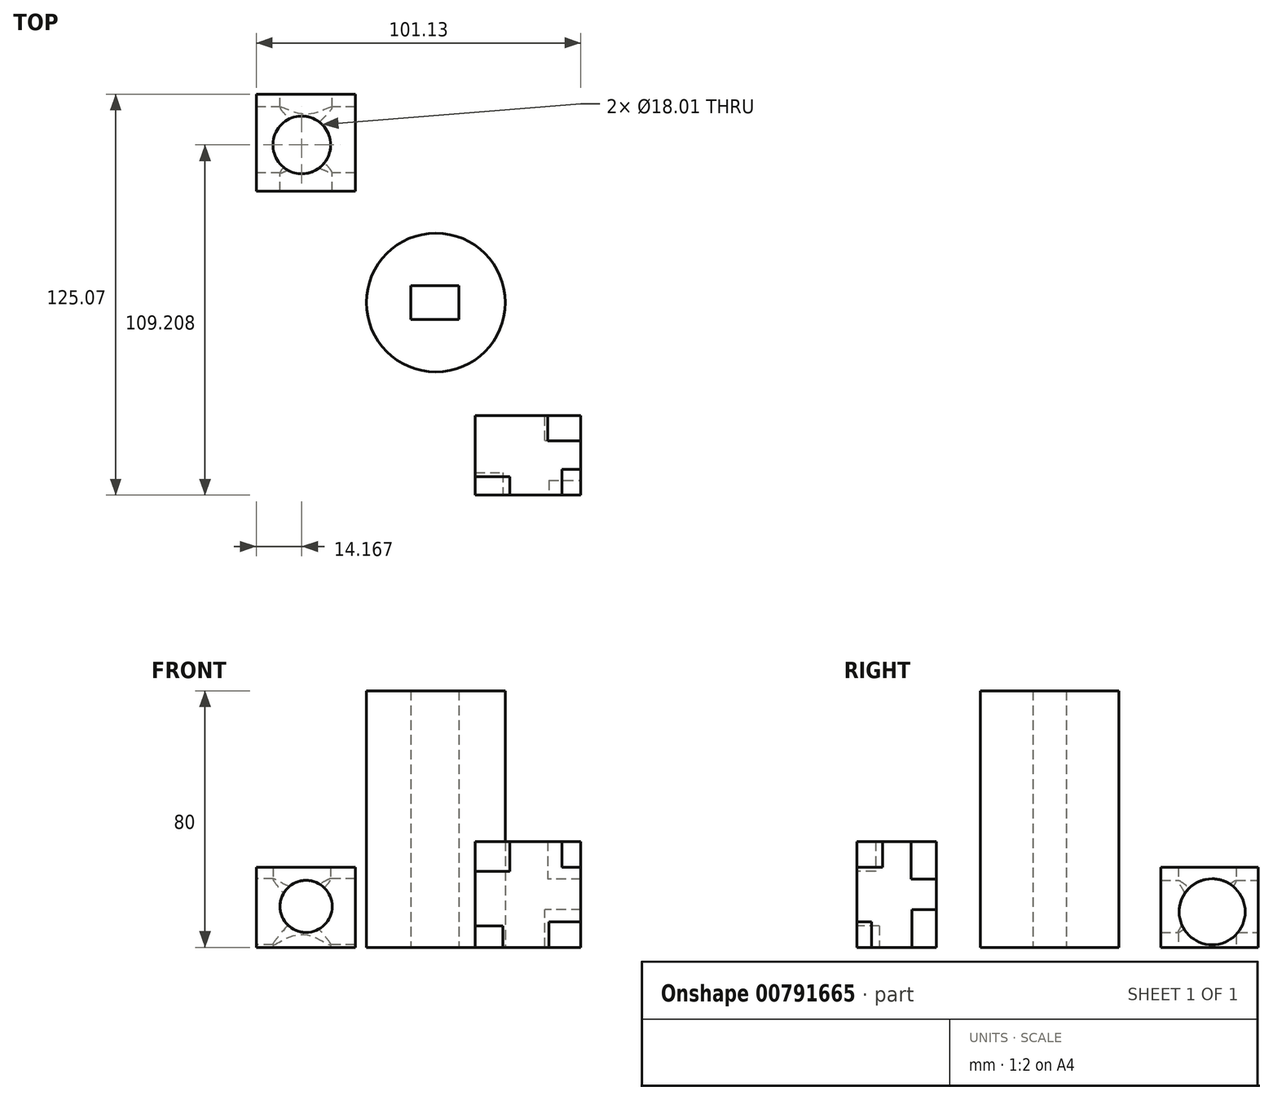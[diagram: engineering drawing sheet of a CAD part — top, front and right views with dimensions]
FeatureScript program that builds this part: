
annotation { "Feature Type Name" : "Feature", "Feature Type Description" : "" }
export const myFeature = defineFeature(function(context is Context, id is Id, definition is map)
    precondition{}
    {
        {
            var Q0;
            Q0=qCreatedBy(makeId("Top.planeOp"),FACE);
            var sketch = newSketch(context, id + "F0", { "sketchPlane" : qUnion([Q0])});
            skCircle(sketch, "E0", {"center": v(0, 0) * mm, "radius": 21.63 * mm});
            skLineSegment(sketch, "E1.bottom", {"start": v(-7.8, 5.24) * mm, "end": v(7.22, 5.24) * mm});
            skLineSegment(sketch, "E1.top", {"start": v(-7.8, -5.24) * mm, "end": v(7.22, -5.24) * mm});
            skLineSegment(sketch, "E1.left", {"start": v(-7.8, 5.24) * mm, "end": v(-7.8, -5.24) * mm});
            skLineSegment(sketch, "E1.right", {"start": v(7.22, 5.24) * mm, "end": v(7.22, -5.24) * mm});
            skSolve(sketch);
        }
        {
            var Q0;
            Q0=makeQuery(id+"F0.imprint","IMPRINT",FACE,{"disambiguationData":[TD([[makeQuery(id+"F0.imprint","IMPRINT",EDGE,{"derivedFrom":sQuery(id+"F0.wireOp",EDGE,"E0")}),1.0]])]});
            extrude(context, id + "F1", {"entities" : qUnion([Q0]), "depth" : 80 * mm, "offsetDistance" : 25 * mm});
        }
        {
            var Q0;
            Q0=qCreatedBy(makeId("Top.planeOp"),FACE);
            var sketch = newSketch(context, id + "F2", { "sketchPlane" : qUnion([Q0])});
            skLineSegment(sketch, "E2.bottom", {"start": v(-55.95, 65.01) * mm, "end": v(-25.07, 65.01) * mm});
            skLineSegment(sketch, "E2.top", {"start": v(-55.95, 34.7) * mm, "end": v(-25.07, 34.7) * mm});
            skLineSegment(sketch, "E2.left", {"start": v(-55.95, 65.01) * mm, "end": v(-55.95, 34.7) * mm});
            skLineSegment(sketch, "E2.right", {"start": v(-25.07, 65.01) * mm, "end": v(-25.07, 34.7) * mm});
            skCircle(sketch, "E3", {"center": v(-41.78, 49.15) * mm, "radius": 9 * mm});
            skSolve(sketch);
        }
        {
            var Q0;
            Q0=makeQuery(id+"F2.imprint","IMPRINT",FACE,{"disambiguationData":[TD([[makeQuery(id+"F2.imprint","IMPRINT",EDGE,{"derivedFrom":sQuery(id+"F2.wireOp",EDGE,"E2.bottom")}),-1.0]])]});
            extrude(context, id + "F3", {"entities" : qUnion([Q0]), "depth" : 25 * mm, "offsetDistance" : 25 * mm});
        }
        {
            var Q0;
            Q0=makeQuery(id+"F3.opExtrude","SWEPT_FACE",FACE,{"disambiguationData":[OSD([sQuery(id+"F2.wireOp",EDGE,"E2.left")])]});
            var sketch = newSketch(context, id + "F4", { "sketchPlane" : qUnion([Q0])});
            skCircle(sketch, "E4", {"center": v(-50.7, 11.09) * mm, "radius": 10.29 * mm});
            skSolve(sketch);
        }
        {
            var Q0;
            Q0=makeQuery(id+"F4.imprint","IMPRINT",FACE,{"disambiguationData":[TD([[makeQuery(id+"F4.imprint","IMPRINT",EDGE,{"derivedFrom":sQuery(id+"F4.wireOp",EDGE,"E4")}),1.0]])]});
            var Q1;
            Q1=sQuery(id+"F4.wireOp",EDGE,"E4");
            extrude(context, id + "F5", {"entities" : qUnion([Q0]), "operationType" : NewBodyOperationType.REMOVE, "surfaceEntities" : qUnion([Q1]), "oppositeDirection" : true, "depth" : 33.2 * mm, "offsetDistance" : 25 * mm});
        }
        {
            var Q0;
            Q0=makeQuery(id+"F3.opExtrude","SWEPT_FACE",FACE,{"disambiguationData":[OSD([sQuery(id+"F2.wireOp",EDGE,"E2.bottom")])]});
            var sketch = newSketch(context, id + "F6", { "sketchPlane" : qUnion([Q0])});
            skCircle(sketch, "E5", {"center": v(40.44, 12.77) * mm, "radius": 8.12 * mm});
            skSolve(sketch);
        }
        {
            var Q0;
            Q0=makeQuery(id+"F6.imprint","IMPRINT",FACE,{"disambiguationData":[TD([[makeQuery(id+"F6.imprint","IMPRINT",EDGE,{"derivedFrom":sQuery(id+"F6.wireOp",EDGE,"E5")}),1.0]])]});
            extrude(context, id + "F7", {"entities" : qUnion([Q0]), "operationType" : NewBodyOperationType.REMOVE, "oppositeDirection" : true, "depth" : 45.1 * mm, "offsetDistance" : 25 * mm});
        }
        {
            var Q0;
            Q0=qCreatedBy(makeId("Top.planeOp"),FACE);
            var sketch = newSketch(context, id + "F8", { "sketchPlane" : qUnion([Q0])});
            skLineSegment(sketch, "E6.bottom", {"start": v(12.32, -35.27) * mm, "end": v(45.18, -35.27) * mm});
            skLineSegment(sketch, "E6.top", {"start": v(12.32, -60.76) * mm, "end": v(45.18, -60.76) * mm});
            skLineSegment(sketch, "E6.left", {"start": v(12.32, -35.27) * mm, "end": v(12.32, -60.76) * mm});
            skLineSegment(sketch, "E6.right", {"start": v(45.18, -35.27) * mm, "end": v(45.18, -60.76) * mm});
            skSolve(sketch);
        }
        {
            var Q0;
            Q0 = qSketchRegion(id + "F8", true);
            extrude(context, id + "F9", {"entities" : qUnion([Q0]), "depth" : 33 * mm, "offsetDistance" : 25 * mm});
        }
        {
            var Q0;
            Q0=makeQuery(id+"F9.opExtrude","SWEPT_FACE",FACE,{"disambiguationData":[OSD([sQuery(id+"F8.wireOp",EDGE,"E6.top")])]});
            var sketch = newSketch(context, id + "F10", { "sketchPlane" : qUnion([Q0])});
            skLineSegment(sketch, "E7.bottom", {"start": v(45.18, 0) * mm, "end": v(35.27, 0) * mm});
            skLineSegment(sketch, "E7.top", {"start": v(45.18, 7.92) * mm, "end": v(35.27, 7.92) * mm});
            skLineSegment(sketch, "E7.left", {"start": v(45.18, 0) * mm, "end": v(45.18, 7.92) * mm});
            skLineSegment(sketch, "E7.right", {"start": v(35.27, 0) * mm, "end": v(35.27, 7.92) * mm});
            skSolve(sketch);
        }
        {
            var Q0;
            Q0 = qSketchRegion(id + "F10", true);
            extrude(context, id + "F11", {"entities" : qUnion([Q0]), "operationType" : NewBodyOperationType.REMOVE, "oppositeDirection" : true, "depth" : 5.3 * mm, "offsetDistance" : 25 * mm});
        }
        {
            var Q0;
            Q0=makeQuery(id+"F9.opExtrude","SWEPT_FACE",FACE,{"disambiguationData":[OSD([sQuery(id+"F8.wireOp",EDGE,"E6.top")])]});
            var sketch = newSketch(context, id + "F12", { "sketchPlane" : qUnion([Q0])});
            skLineSegment(sketch, "E8.bottom", {"start": v(12.32, 0) * mm, "end": v(20.93, 0) * mm});
            skLineSegment(sketch, "E8.top", {"start": v(12.32, 6.74) * mm, "end": v(20.93, 6.74) * mm});
            skLineSegment(sketch, "E8.left", {"start": v(12.32, 0) * mm, "end": v(12.32, 6.74) * mm});
            skLineSegment(sketch, "E8.right", {"start": v(20.93, 0) * mm, "end": v(20.93, 6.74) * mm});
            skSolve(sketch);
        }
        {
            var Q0;
            Q0 = qSketchRegion(id + "F12", true);
            extrude(context, id + "F13", {"entities" : qUnion([Q0]), "operationType" : NewBodyOperationType.REMOVE, "oppositeDirection" : true, "depth" : 7.7 * mm, "offsetDistance" : 25 * mm});
        }
        {
            var Q0;
            Q0=makeQuery(id+"F9.opExtrude","SWEPT_FACE",FACE,{"disambiguationData":[OSD([sQuery(id+"F8.wireOp",EDGE,"E6.top")])]});
            var sketch = newSketch(context, id + "F14", { "sketchPlane" : qUnion([Q0])});
            skLineSegment(sketch, "E9.bottom", {"start": v(39.37, 33) * mm, "end": v(45.18, 33) * mm});
            skLineSegment(sketch, "E9.top", {"start": v(39.37, 24.91) * mm, "end": v(45.18, 24.91) * mm});
            skLineSegment(sketch, "E9.left", {"start": v(39.37, 33) * mm, "end": v(39.37, 24.91) * mm});
            skLineSegment(sketch, "E9.right", {"start": v(45.18, 33) * mm, "end": v(45.18, 24.91) * mm});
            skSolve(sketch);
        }
        {
            var Q0;
            Q0 = qSketchRegion(id + "F14", true);
            extrude(context, id + "F15", {"entities" : qUnion([Q0]), "operationType" : NewBodyOperationType.REMOVE, "oppositeDirection" : true, "depth" : 8.7 * mm, "offsetDistance" : 25 * mm});
        }
        {
            var Q0;
            Q0=makeQuery(id+"F9.opExtrude","SWEPT_FACE",FACE,{"disambiguationData":[OSD([sQuery(id+"F8.wireOp",EDGE,"E6.top")])]});
            var sketch = newSketch(context, id + "F16", { "sketchPlane" : qUnion([Q0])});
            skLineSegment(sketch, "E10.bottom", {"start": v(12.32, 33) * mm, "end": v(23.14, 33) * mm});
            skLineSegment(sketch, "E10.top", {"start": v(12.32, 23.99) * mm, "end": v(23.14, 23.99) * mm});
            skLineSegment(sketch, "E10.left", {"start": v(12.32, 33) * mm, "end": v(12.32, 23.99) * mm});
            skLineSegment(sketch, "E10.right", {"start": v(23.14, 33) * mm, "end": v(23.14, 23.99) * mm});
            skSolve(sketch);
        }
        {
            var Q0;
            Q0=makeQuery(id+"F16.imprint","IMPRINT",FACE,{"disambiguationData":[TD([[makeQuery(id+"F16.imprint","IMPRINT",EDGE,{"derivedFrom":sQuery(id+"F16.wireOp",EDGE,"E10.bottom")}),-1.0]])]});
            var Q1;
            Q1=makeQuery(id+"F9.opExtrude","SWEPT_FACE",FACE,{"disambiguationData":[OSD([sQuery(id+"F8.wireOp",EDGE,"E6.bottom")])]});
            var Q2;
            {var subQ4=sQuery(id+"F16.wireOp",EDGE,"E10.top");Q2=makeQuery(id+"F16.imprint","IMPRINT",FACE,{"disambiguationData":[TD([[makeQuery(id+"F16.imprint","IMPRINT",EDGE,{"derivedFrom":subQ4}),-1.0]])]});}
            var Q3;
            Q3=makeQuery(id+"F9.opExtrude","SWEPT_FACE",FACE,{"disambiguationData":[OSD([sQuery(id+"F8.wireOp",EDGE,"E6.top")])]});
            var Q4;
            Q4=makeQuery(id+"F3.opExtrude","SWEPT_FACE",FACE,{"disambiguationData":[OSD([sQuery(id+"F2.wireOp",EDGE,"E2.bottom")])]});
            extrude(context, id + "F17", {"entities" : qUnion([Q0, Q1, Q2, Q3, Q4]), "operationType" : NewBodyOperationType.REMOVE, "oppositeDirection" : true, "depth" : 0.7 * mm, "offsetDistance" : 25 * mm});
        }
        {
            var Q0;
            Q0=makeQuery(id+"F17.boolean.opBoolean","COPY",FACE,{"derivedFrom":makeQuery(id+"F17.opExtrude","CAP_FACE",FACE,{"disambiguationData":[OSD([sQuery(id+"F8.wireOp",EDGE,"E6.top"),sQuery(id+"F8.wireOp",EDGE,"E6.left"),sQuery(id+"F8.wireOp",EDGE,"E6.right"),sQuery(id+"F10.wireOp",EDGE,"E7.top"),sQuery(id+"F10.wireOp",EDGE,"E7.right"),sQuery(id+"F12.wireOp",EDGE,"E8.top"),sQuery(id+"F12.wireOp",EDGE,"E8.right"),sQuery(id+"F14.wireOp",EDGE,"E9.top"),sQuery(id+"F14.wireOp",EDGE,"E9.left"),sQuery(id+"F16.wireOp",EDGE,"E10.bottom"),sQuery(id+"F16.wireOp",EDGE,"E10.left")])],"isStart":false})});
            var sketch = newSketch(context, id + "F18", { "sketchPlane" : qUnion([Q0])});
            skLineSegment(sketch, "E11.bottom", {"start": v(12.32, 33) * mm, "end": v(23.06, 33) * mm});
            skLineSegment(sketch, "E11.top", {"start": v(12.32, 23.65) * mm, "end": v(23.06, 23.65) * mm});
            skLineSegment(sketch, "E11.left", {"start": v(12.32, 33) * mm, "end": v(12.32, 23.65) * mm});
            skLineSegment(sketch, "E11.right", {"start": v(23.06, 33) * mm, "end": v(23.06, 23.65) * mm});
            skSolve(sketch);
        }
        {
            var Q0;
            Q0 = qSketchRegion(id + "F18", true);
            extrude(context, id + "F19", {"entities" : qUnion([Q0]), "operationType" : NewBodyOperationType.REMOVE, "oppositeDirection" : true, "depth" : 5.8 * mm, "offsetDistance" : 25 * mm});
        }
        {
            var Q0;
            Q0=makeQuery(id+"F9.opExtrude","SWEPT_FACE",FACE,{"disambiguationData":[OSD([sQuery(id+"F8.wireOp",EDGE,"E6.bottom")])]});
            var sketch = newSketch(context, id + "F20", { "sketchPlane" : qUnion([Q0])});
            skLineSegment(sketch, "E12.bottom", {"start": v(-45.18, 33) * mm, "end": v(-34.72, 33) * mm});
            skLineSegment(sketch, "E12.top", {"start": v(-45.18, 20.28) * mm, "end": v(-34.72, 20.28) * mm});
            skLineSegment(sketch, "E12.left", {"start": v(-45.18, 33) * mm, "end": v(-45.18, 20.28) * mm});
            skLineSegment(sketch, "E12.right", {"start": v(-34.72, 33) * mm, "end": v(-34.72, 20.28) * mm});
            skSolve(sketch);
        }
        {
            var Q0;
            Q0 = qSketchRegion(id + "F20", true);
            extrude(context, id + "F21", {"entities" : qUnion([Q0]), "operationType" : NewBodyOperationType.REMOVE, "depth" : 5.4 * mm, "offsetDistance" : 25 * mm});
        }
        {
            var Q0;
            Q0=makeQuery(id+"F9.opExtrude","SWEPT_FACE",FACE,{"disambiguationData":[OSD([sQuery(id+"F8.wireOp",EDGE,"E6.bottom")])]});
            var sketch = newSketch(context, id + "F22", { "sketchPlane" : qUnion([Q0])});
            skLineSegment(sketch, "E13.bottom", {"start": v(-45.18, 33) * mm, "end": v(-34.86, 33) * mm});
            skLineSegment(sketch, "E13.top", {"start": v(-45.18, 21.24) * mm, "end": v(-34.86, 21.24) * mm});
            skLineSegment(sketch, "E13.left", {"start": v(-45.18, 33) * mm, "end": v(-45.18, 21.24) * mm});
            skLineSegment(sketch, "E13.right", {"start": v(-34.86, 33) * mm, "end": v(-34.86, 21.24) * mm});
            skSolve(sketch);
        }
        {
            var Q0;
            Q0=makeQuery(id+"F22.imprint","IMPRINT",FACE,{"disambiguationData":[TD([[makeQuery(id+"F22.imprint","IMPRINT",EDGE,{"derivedFrom":sQuery(id+"F22.wireOp",EDGE,"E13.bottom")}),1.0]])]});
            extrude(context, id + "F23", {"entities" : qUnion([Q0]), "operationType" : NewBodyOperationType.REMOVE, "oppositeDirection" : true, "depth" : 7.9 * mm, "offsetDistance" : 25 * mm});
        }
        {
            var Q0;
            Q0=makeQuery(id+"F9.opExtrude","SWEPT_FACE",FACE,{"disambiguationData":[OSD([sQuery(id+"F8.wireOp",EDGE,"E6.bottom")])]});
            var sketch = newSketch(context, id + "F24", { "sketchPlane" : qUnion([Q0])});
            skLineSegment(sketch, "E14.bottom", {"start": v(-45.18, 0) * mm, "end": v(-33.92, 0) * mm});
            skLineSegment(sketch, "E14.top", {"start": v(-45.18, 11.78) * mm, "end": v(-33.92, 11.78) * mm});
            skLineSegment(sketch, "E14.left", {"start": v(-45.18, 0) * mm, "end": v(-45.18, 11.78) * mm});
            skLineSegment(sketch, "E14.right", {"start": v(-33.92, 0) * mm, "end": v(-33.92, 11.78) * mm});
            skSolve(sketch);
        }
        {
            var Q0;
            Q0=makeQuery(id+"F24.imprint","IMPRINT",FACE,{"disambiguationData":[TD([[makeQuery(id+"F24.imprint","IMPRINT",EDGE,{"derivedFrom":sQuery(id+"F24.wireOp",EDGE,"E14.bottom")}),-1.0]])]});
            extrude(context, id + "F25", {"entities" : qUnion([Q0]), "operationType" : NewBodyOperationType.REMOVE, "oppositeDirection" : true, "depth" : 7.7 * mm, "offsetDistance" : 25 * mm});
        }
    });
